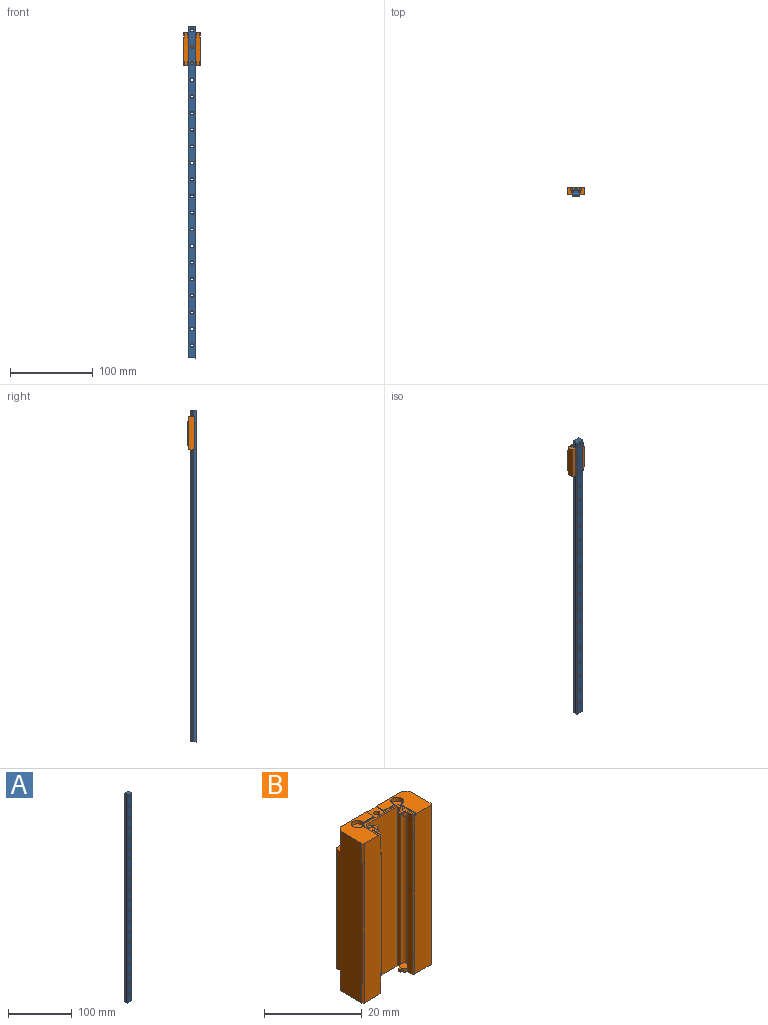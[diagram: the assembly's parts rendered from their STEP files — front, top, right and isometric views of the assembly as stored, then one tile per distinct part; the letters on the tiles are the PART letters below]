
ASSEMBLY  parts=2 mates=1
PART A: 122 faces, bbox 9x6.5x400 mm
  f0: cylinder r=1.75mm len=3.5mm, axis (0,1,0), area 30.8mm2, adj f45,f58
  f1: cylinder r=1.75mm len=3.5mm, axis (0,1,0), area 30.8mm2, adj f43,f56
  f2: cylinder r=1.75mm len=3.5mm, axis (0,1,0), area 30.8mm2, adj f41,f54
  f3: cylinder r=1.75mm len=3.5mm, axis (0,1,0), area 30.8mm2, adj f39,f52
  f4: cylinder r=1.75mm len=3.5mm, axis (0,1,0), area 30.8mm2, adj f37,f50
  f5: cylinder r=1.75mm len=3.5mm, axis (0,1,0), area 30.8mm2, adj f35,f48
  f6: cylinder r=1.75mm len=3.5mm, axis (0,1,0), area 30.8mm2, adj f33,f46
  f7: cylinder r=1.75mm len=3.5mm, axis (0,1,0), area 30.8mm2, adj f29,f30
  f8: cylinder r=1mm len=400mm, axis (0,0,-1), area 461.1mm2, adj f9,f27,f72,f121
  f9: plane 400x0.5mm, normal (0,-1,0), area 200mm2, adj f8,f10,f72,f121
  f10: plane 400x0.5mm, normal (-1,0,0), area 200mm2, adj f9,f11,f72,f121
  f11: plane 400x0.47mm, normal (0,1,0), area 187.1mm2, adj f10,f12,f72,f121
  f12: cylinder r=1mm len=400mm, axis (0,0,-1), area 512.8mm2, adj f11,f13,f72,f121
  f13: plane 400x3.51mm, normal (-1,0,0), area 1402mm2, adj f12,f14,f72,f121
  f14: plane 400x0.2mm, normal (-0.71,-0.71,0), area 113.1mm2, adj f13,f15,f72,f121
  f15: plane 400x8.6mm, normal (0,-1,0), area 3201.1mm2, adj f14,f16,f30,f46,f48,f50,f52,f54
  f16: plane 400x0.2mm, normal (0.71,-0.71,0), area 113.1mm2, adj f15,f17,f72,f121
  f17: plane 400x3.51mm, normal (1,0,0), area 1402mm2, adj f16,f18,f72,f121
  f18: cylinder r=1mm len=400mm, axis (0,0,-1), area 512.8mm2, adj f17,f19,f72,f121
  f19: plane 400x0.47mm, normal (0,1,0), area 187.1mm2, adj f18,f20,f72,f121
  f20: plane 400x0.5mm, normal (1,0,0), area 200mm2, adj f19,f21,f72,f121
  f21: plane 400x0.5mm, normal (0,-1,0), area 200mm2, adj f20,f22,f72,f121
  f22: cylinder r=1mm len=400mm, axis (0,0,-1), area 461.1mm2, adj f21,f23,f72,f121
  f23: plane 400x0.61mm, normal (1,0,0), area 242mm2, adj f22,f24,f72,f121
  f24: plane 400x0.2mm, normal (0.71,0.71,0), area 113.1mm2, adj f23,f25,f72,f121
  f25: plane 400x8.6mm, normal (0,1,0), area 2796.6mm2, adj f24,f26,f31,f47,f49,f51,f53,f55
  f26: plane 400x0.2mm, normal (-0.71,0.71,0), area 113.1mm2, adj f25,f27,f72,f121
  f27: plane 400x0.61mm, normal (-1,0,0), area 242mm2, adj f8,f26,f72,f121
  f28: cylinder r=3mm len=6mm, axis (0,1,0), area 62.2mm2, adj f29,f31
  f29: plane 6x6mm, normal (0,1,0), area 18.7mm2, adj f7,f28
  f30: cone r=1.75mm half-angle=45deg, axis (0,-1,0), area 3.3mm2, adj f7,f15
  f31: cone r=3mm half-angle=45deg, axis (0,1,0), area 5.5mm2, adj f25,f28
  f32: cylinder r=3mm len=6mm, axis (0,1,0), area 62.2mm2, adj f33,f47
  f33: plane 6x6mm, normal (0,1,0), area 18.7mm2, adj f6,f32
  f34: cylinder r=3mm len=6mm, axis (0,1,0), area 62.2mm2, adj f35,f49
  f35: plane 6x6mm, normal (0,1,0), area 18.7mm2, adj f5,f34
  f36: cylinder r=3mm len=6mm, axis (0,1,0), area 62.2mm2, adj f37,f51
  f37: plane 6x6mm, normal (0,1,0), area 18.7mm2, adj f4,f36
  f38: cylinder r=3mm len=6mm, axis (0,1,0), area 62.2mm2, adj f39,f53
  f39: plane 6x6mm, normal (0,1,0), area 18.7mm2, adj f3,f38
  f40: cylinder r=3mm len=6mm, axis (0,1,0), area 62.2mm2, adj f41,f55
  f41: plane 6x6mm, normal (0,1,0), area 18.7mm2, adj f2,f40
  f42: cylinder r=3mm len=6mm, axis (0,1,0), area 62.2mm2, adj f43,f57
  f43: plane 6x6mm, normal (0,1,0), area 18.7mm2, adj f1,f42
  f44: cylinder r=3mm len=6mm, axis (0,1,0), area 62.2mm2, adj f45,f59
  f45: plane 6x6mm, normal (0,1,0), area 18.7mm2, adj f0,f44
  f46: cone r=1.75mm half-angle=45deg, axis (0,-1,0), area 3.3mm2, adj f6,f15
  f47: cone r=3mm half-angle=45deg, axis (0,1,0), area 5.5mm2, adj f25,f32
  f48: cone r=1.75mm half-angle=45deg, axis (0,-1,0), area 3.3mm2, adj f5,f15
  f49: cone r=3mm half-angle=45deg, axis (0,1,0), area 5.5mm2, adj f25,f34
  f50: cone r=1.75mm half-angle=45deg, axis (0,-1,0), area 3.3mm2, adj f4,f15
  f51: cone r=3mm half-angle=45deg, axis (0,1,0), area 5.5mm2, adj f25,f36
  f52: cone r=1.75mm half-angle=45deg, axis (0,-1,0), area 3.3mm2, adj f3,f15
  f53: cone r=3mm half-angle=45deg, axis (0,1,0), area 5.5mm2, adj f25,f38
  f54: cone r=1.75mm half-angle=45deg, axis (0,-1,0), area 3.3mm2, adj f2,f15
  f55: cone r=3mm half-angle=45deg, axis (0,1,0), area 5.5mm2, adj f25,f40
  f56: cone r=1.75mm half-angle=45deg, axis (0,-1,0), area 3.3mm2, adj f1,f15
  f57: cone r=3mm half-angle=45deg, axis (0,1,0), area 5.5mm2, adj f25,f42
  f58: cone r=1.75mm half-angle=45deg, axis (0,-1,0), area 3.3mm2, adj f0,f15
  f59: cone r=3mm half-angle=45deg, axis (0,1,0), area 5.5mm2, adj f25,f44
  f60: cylinder r=1.75mm len=3.5mm, axis (0,1,0), area 30.8mm2, adj f98,f119
  f61: cylinder r=1.75mm len=3.5mm, axis (0,1,0), area 30.8mm2, adj f96,f117
  f62: cylinder r=1.75mm len=3.5mm, axis (0,1,0), area 30.8mm2, adj f94,f115
  f63: cylinder r=1.75mm len=3.5mm, axis (0,1,0), area 30.8mm2, adj f92,f113
  f64: cylinder r=1.75mm len=3.5mm, axis (0,1,0), area 30.8mm2, adj f90,f111
  f65: cylinder r=1.75mm len=3.5mm, axis (0,1,0), area 30.8mm2, adj f88,f109
  f66: cylinder r=1.75mm len=3.5mm, axis (0,1,0), area 30.8mm2, adj f86,f107
  f67: cylinder r=1.75mm len=3.5mm, axis (0,1,0), area 30.8mm2, adj f84,f105
  f68: cylinder r=1.75mm len=3.5mm, axis (0,1,0), area 30.8mm2, adj f82,f103
  f69: cylinder r=1.75mm len=3.5mm, axis (0,1,0), area 30.8mm2, adj f80,f101
  f70: cylinder r=1.75mm len=3.5mm, axis (0,1,0), area 30.8mm2, adj f78,f99
  f71: cylinder r=1.75mm len=3.5mm, axis (0,1,0), area 30.8mm2, adj f74,f75
  f72: plane 9x6.5mm, normal (0,0,-1), area 55.2mm2, adj f8,f9,f10,f11,f12,f13,f14,f15
  f73: cylinder r=3mm len=6mm, axis (0,1,0), area 62.2mm2, adj f74,f76
  f74: plane 6x6mm, normal (0,1,0), area 18.7mm2, adj f71,f73
  f75: cone r=1.75mm half-angle=45deg, axis (0,-1,0), area 3.3mm2, adj f15,f71
  f76: cone r=3mm half-angle=45deg, axis (0,1,0), area 5.5mm2, adj f25,f73
  f77: cylinder r=3mm len=6mm, axis (0,1,0), area 62.2mm2, adj f78,f100
  f78: plane 6x6mm, normal (0,1,0), area 18.7mm2, adj f70,f77
  f79: cylinder r=3mm len=6mm, axis (0,1,0), area 62.2mm2, adj f80,f102
  f80: plane 6x6mm, normal (0,1,0), area 18.7mm2, adj f69,f79
  f81: cylinder r=3mm len=6mm, axis (0,1,0), area 62.2mm2, adj f82,f104
  f82: plane 6x6mm, normal (0,1,0), area 18.7mm2, adj f68,f81
  f83: cylinder r=3mm len=6mm, axis (0,1,0), area 62.2mm2, adj f84,f106
  f84: plane 6x6mm, normal (0,1,0), area 18.7mm2, adj f67,f83
  f85: cylinder r=3mm len=6mm, axis (0,1,0), area 62.2mm2, adj f86,f108
  f86: plane 6x6mm, normal (0,1,0), area 18.7mm2, adj f66,f85
  f87: cylinder r=3mm len=6mm, axis (0,1,0), area 62.2mm2, adj f88,f110
  f88: plane 6x6mm, normal (0,1,0), area 18.7mm2, adj f65,f87
  f89: cylinder r=3mm len=6mm, axis (0,1,0), area 62.2mm2, adj f90,f112
  f90: plane 6x6mm, normal (0,1,0), area 18.7mm2, adj f64,f89
  f91: cylinder r=3mm len=6mm, axis (0,1,0), area 62.2mm2, adj f92,f114
  f92: plane 6x6mm, normal (0,1,0), area 18.7mm2, adj f63,f91
  f93: cylinder r=3mm len=6mm, axis (0,1,0), area 62.2mm2, adj f94,f116
  f94: plane 6x6mm, normal (0,1,0), area 18.7mm2, adj f62,f93
  f95: cylinder r=3mm len=6mm, axis (0,1,0), area 62.2mm2, adj f96,f118
  f96: plane 6x6mm, normal (0,1,0), area 18.7mm2, adj f61,f95
  f97: cylinder r=3mm len=6mm, axis (0,1,0), area 62.2mm2, adj f98,f120
  f98: plane 6x6mm, normal (0,1,0), area 18.7mm2, adj f60,f97
  f99: cone r=1.75mm half-angle=45deg, axis (0,-1,0), area 3.3mm2, adj f15,f70
  f100: cone r=3mm half-angle=45deg, axis (0,1,0), area 5.5mm2, adj f25,f77
  f101: cone r=1.75mm half-angle=45deg, axis (0,-1,0), area 3.3mm2, adj f15,f69
  f102: cone r=3mm half-angle=45deg, axis (0,1,0), area 5.5mm2, adj f25,f79
  f103: cone r=1.75mm half-angle=45deg, axis (0,-1,0), area 3.3mm2, adj f15,f68
  f104: cone r=3mm half-angle=45deg, axis (0,1,0), area 5.5mm2, adj f25,f81
  f105: cone r=1.75mm half-angle=45deg, axis (0,-1,0), area 3.3mm2, adj f15,f67
  f106: cone r=3mm half-angle=45deg, axis (0,1,0), area 5.5mm2, adj f25,f83
  f107: cone r=1.75mm half-angle=45deg, axis (0,-1,0), area 3.3mm2, adj f15,f66
  f108: cone r=3mm half-angle=45deg, axis (0,1,0), area 5.5mm2, adj f25,f85
  f109: cone r=1.75mm half-angle=45deg, axis (0,-1,0), area 3.3mm2, adj f15,f65
  f110: cone r=3mm half-angle=45deg, axis (0,1,0), area 5.5mm2, adj f25,f87
  f111: cone r=1.75mm half-angle=45deg, axis (0,-1,0), area 3.3mm2, adj f15,f64
  f112: cone r=3mm half-angle=45deg, axis (0,1,0), area 5.5mm2, adj f25,f89
  f113: cone r=1.75mm half-angle=45deg, axis (0,-1,0), area 3.3mm2, adj f15,f63
  f114: cone r=3mm half-angle=45deg, axis (0,1,0), area 5.5mm2, adj f25,f91
  f115: cone r=1.75mm half-angle=45deg, axis (0,-1,0), area 3.3mm2, adj f15,f62
  f116: cone r=3mm half-angle=45deg, axis (0,1,0), area 5.5mm2, adj f25,f93
  f117: cone r=1.75mm half-angle=45deg, axis (0,-1,0), area 3.3mm2, adj f15,f61
  f118: cone r=3mm half-angle=45deg, axis (0,1,0), area 5.5mm2, adj f25,f95
  f119: cone r=1.75mm half-angle=45deg, axis (0,-1,0), area 3.3mm2, adj f15,f60
  f120: cone r=3mm half-angle=45deg, axis (0,1,0), area 5.5mm2, adj f25,f97
  f121: plane 9x6.5mm, normal (0,0,1), area 55.2mm2, adj f8,f9,f10,f11,f12,f13,f14,f15
PART B: 137 faces, bbox 20x8x39.9 mm
  f0: plane 0.4x0.4mm, normal (0,0,1), area 0mm2, adj f17,f18,f36,f114
  f1: plane 5.5x1.3mm, normal (0,0,1), area 2.1mm2, adj f18,f24,f25,f26,f37,f110
  f2: plane 5.5x1.3mm, normal (0,0,1), area 2.1mm2, adj f20,f23,f25,f27,f34,f109
  f3: plane 0.4x0.4mm, normal (0,0,1), area 0mm2, adj f19,f20,f35,f112
  f4: plane 0.4x0.4mm, normal (0,0,1), area 0mm2, adj f19,f28,f39,f111
  f5: plane 0.4x0.4mm, normal (0,0,1), area 0mm2, adj f17,f21,f38,f113
  f6: plane 0.4x0.4mm, normal (0,0,-1), area 0mm2, adj f17,f21,f38,f50
  f7: plane 0.4x0.4mm, normal (0,0,-1), area 0mm2, adj f19,f28,f39,f51
  f8: plane 0.4x0.4mm, normal (0,0,-1), area 0mm2, adj f19,f20,f35,f52
  f9: plane 5.5x1.3mm, normal (0,0,-1), area 2.1mm2, adj f20,f23,f25,f27,f34,f48
  f10: plane 5.5x1.3mm, normal (0,0,-1), area 2.1mm2, adj f18,f24,f25,f26,f37,f47
  f11: plane 3x3mm, normal (0,1,0), area 7.1mm2, adj f13
  f12: plane 3x3mm, normal (0,1,0), area 7.1mm2, adj f14
  f13: cylinder r=1.5mm len=3mm, axis (0,1,0), area 25.4mm2, adj f11,f15
  f14: cylinder r=1.5mm len=3mm, axis (0,1,0), area 25.4mm2, adj f12,f16
  f15: cone r=1.5mm half-angle=45deg, axis (0,1,0), area 4.4mm2, adj f13,f23
  f16: cone r=1.5mm half-angle=45deg, axis (0,1,0), area 4.4mm2, adj f14,f24
  f17: plane 39.9x4.9mm, normal (0,-1,0), area 193.3mm2, adj f0,f5,f6,f36,f38,f46,f49,f50
  f18: plane 39.9x7.4mm, normal (-1,0,0), area 284.3mm2, adj f0,f1,f10,f36,f37,f46,f47,f49
  f19: plane 39.9x4.9mm, normal (0,-1,0), area 193.3mm2, adj f3,f4,f7,f8,f35,f39,f51,f52
  f20: plane 39.9x7.4mm, normal (1,0,0), area 284.3mm2, adj f2,f3,f8,f9,f34,f35,f48,f52
  f21: plane 39.9x1.41mm, normal (1,0,0), area 55.1mm2, adj f5,f6,f31,f38,f50,f56,f64,f95
  f22: plane 39.9x0.81mm, normal (-1,0,0), area 32.1mm2, adj f29,f33,f56,f59,f95,f98
  f23: plane 29.9x4.9mm, normal (0,1,0), area 126.2mm2, adj f2,f9,f15,f27,f34,f44
  f24: plane 29.9x4.9mm, normal (0,1,0), area 126.2mm2, adj f1,f10,f16,f26,f37,f45
  f25: plane 39.9x18mm, normal (0,1,0), area 448mm2, adj f1,f2,f9,f10,f26,f27,f47,f48
  f26: plane 29.9x0.3mm, normal (0.71,0.71,0), area 12.7mm2, adj f1,f10,f24,f25
  f27: plane 29.9x0.3mm, normal (-0.71,0.71,0), area 12.7mm2, adj f2,f9,f23,f25
  f28: plane 39.9x1.41mm, normal (-1,0,0), area 55.1mm2, adj f4,f7,f29,f39,f51,f56,f63,f95
  f29: cylinder r=1mm len=38.1mm, axis (0,0,-1), area 127.3mm2, adj f22,f28,f53,f93
  f30: plane 39.9x0.81mm, normal (1,0,0), area 32.1mm2, adj f31,f33,f56,f68,f95,f107
  f31: cylinder r=1mm len=38.1mm, axis (0,0,-1), area 127.3mm2, adj f21,f30,f54,f92
  f32: cylinder r=0.64mm len=39.5mm, axis (0,0,-1), area 159.8mm2, adj f75,f120
  f33: plane 39.9x9mm, normal (0,-1,0), area 359.1mm2, adj f22,f30,f56,f95
  f34: plane 29.9x0.3mm, normal (0.71,0.71,0), area 12.7mm2, adj f2,f9,f20,f23
  f35: plane 29.9x0.3mm, normal (0.71,-0.71,0), area 12.7mm2, adj f3,f8,f19,f20
  f36: plane 29.9x0.3mm, normal (-0.71,-0.71,0), area 12.7mm2, adj f0,f17,f18,f46
  f37: plane 29.9x0.3mm, normal (-0.71,0.71,0), area 12.7mm2, adj f1,f10,f18,f24
  f38: plane 29.9x0.3mm, normal (0.71,-0.71,0), area 12.7mm2, adj f5,f6,f17,f21
  f39: plane 29.9x0.3mm, normal (-0.71,-0.71,0), area 12.7mm2, adj f4,f7,f19,f28
  f40: plane 3x3mm, normal (0,1,0), area 7.1mm2, adj f42
  f41: plane 3x3mm, normal (0,1,0), area 7.1mm2, adj f43
  f42: cylinder r=1.5mm len=3mm, axis (0,1,0), area 25.4mm2, adj f40,f44
  f43: cylinder r=1.5mm len=3mm, axis (0,1,0), area 25.4mm2, adj f41,f45
  f44: cone r=1.5mm half-angle=45deg, axis (0,1,0), area 4.4mm2, adj f23,f42
  f45: cone r=1.5mm half-angle=45deg, axis (0,1,0), area 4.4mm2, adj f24,f43
  f46: plane 0.4x0.4mm, normal (0,0,-1), area 0mm2, adj f17,f18,f36,f49
  f47: plane 5x1mm, normal (-0.71,0.71,0), area 7.1mm2, adj f10,f18,f25,f58
  f48: plane 5x1mm, normal (0.71,0.71,0), area 7.1mm2, adj f9,f20,f25,f55
  f49: plane 5x0.4mm, normal (-0.71,-0.71,0), area 2.8mm2, adj f17,f18,f46,f58
  f50: plane 5x0.4mm, normal (0.71,-0.71,0), area 2.8mm2, adj f6,f17,f21,f56
  f51: plane 5x0.4mm, normal (-0.71,-0.71,0), area 2.8mm2, adj f7,f19,f28,f56
  f52: plane 5x0.4mm, normal (0.71,-0.71,0), area 2.8mm2, adj f8,f19,f20,f55
  f53: plane 2.47x2mm, normal (0,0,1), area 3.4mm2, adj f29,f59,f60,f61,f62,f63
  f54: plane 2.47x2mm, normal (0,0,1), area 3.4mm2, adj f31,f64,f65,f66,f67,f68
  f55: plane 8.58x7.7mm, normal (0,0,-1), area 38.3mm2, adj f19,f20,f25,f48,f52,f69,f71,f72
  f56: plane 10x5mm, normal (0,0,-1), area 10.9mm2, adj f17,f19,f21,f22,f28,f30,f33,f50
  f57: cylinder r=1.3mm len=2.6mm, axis (0,0,1), area 7.1mm2, adj f56,f58,f73,f74,f75,f78,f79,f82
  f58: plane 8.58x7.7mm, normal (0,0,-1), area 38.3mm2, adj f17,f18,f25,f47,f49,f57,f70,f74
  f59: cylinder r=1mm len=0.9mm, axis (0,0,1), area 1.1mm2, adj f22,f53,f56,f60
  f60: plane 0.9x0.5mm, normal (0,1,0), area 0.4mm2, adj f53,f56,f59,f61
  f61: plane 0.9x0.5mm, normal (-1,0,0), area 0.4mm2, adj f53,f56,f60,f62
  f62: plane 0.9x0.5mm, normal (0,-1,0), area 0.4mm2, adj f53,f56,f61,f63
  f63: cylinder r=1mm len=0.9mm, axis (0,0,1), area 1.1mm2, adj f28,f53,f56,f62
  f64: cylinder r=1mm len=0.9mm, axis (0,0,1), area 1.1mm2, adj f21,f54,f56,f65
  f65: plane 0.9x0.5mm, normal (0,-1,0), area 0.4mm2, adj f54,f56,f64,f66
  f66: plane 0.9x0.5mm, normal (1,0,0), area 0.4mm2, adj f54,f56,f65,f67
  f67: plane 0.9x0.5mm, normal (0,1,0), area 0.4mm2, adj f54,f56,f66,f68
  f68: cylinder r=1mm len=0.9mm, axis (0,0,1), area 1.1mm2, adj f30,f54,f56,f67
  f69: cylinder r=1.3mm len=2.6mm, axis (0,0,1), area 7.1mm2, adj f55,f56,f72,f73,f75,f85,f86,f89
  f70: plane 2.2x0.2mm, normal (1,0,0), area 0.4mm2, adj f25,f58,f74,f75
  f71: plane 2.2x0.2mm, normal (-1,0,0), area 0.4mm2, adj f25,f55,f72,f75
  f72: plane 3.09x0.2mm, normal (0,-1,0), area 0.6mm2, adj f55,f69,f71,f75
  f73: plane 9.63x0.2mm, normal (0,1,0), area 1.9mm2, adj f56,f57,f69,f75
  f74: plane 3.09x0.2mm, normal (0,-1,0), area 0.6mm2, adj f57,f58,f70,f75
  f75: plane 9.63x2.7mm, normal (0,0,-1), area 9.6mm2, adj f25,f32,f57,f69,f70,f71,f72,f73
  f76: plane 0.45x0.2mm, normal (0,1,0), area 0.1mm2, adj f56,f77,f81,f82
  f77: plane 2.2x0.2mm, normal (-1,0,0), area 0.4mm2, adj f17,f56,f76,f82
  f78: plane 4.64x0.2mm, normal (1,0,0), area 0.9mm2, adj f17,f57,f58,f82
  f79: plane 1.65x0.2mm, normal (-1,0,0), area 0.3mm2, adj f56,f57,f80,f82
  f80: plane 0.4x0.2mm, normal (0,-1,0), area 0.1mm2, adj f56,f79,f81,f82
  f81: cylinder r=0.5mm len=1mm, axis (0,0,-1), area 0.3mm2, adj f56,f76,f80,f82
  f82: plane 4.85x1.4mm, normal (0,0,-1), area 3.2mm2, adj f17,f57,f76,f77,f78,f79,f80,f81
  f83: cylinder r=0.5mm len=1mm, axis (0,0,-1), area 0.3mm2, adj f56,f84,f88,f89
  f84: plane 0.4x0.2mm, normal (0,-1,0), area 0.1mm2, adj f56,f83,f85,f89
  f85: plane 1.65x0.2mm, normal (1,0,0), area 0.3mm2, adj f56,f69,f84,f89
  f86: plane 4.64x0.2mm, normal (-1,0,0), area 0.9mm2, adj f19,f55,f69,f89
  f87: plane 2.2x0.2mm, normal (1,0,0), area 0.4mm2, adj f19,f56,f88,f89
  f88: plane 0.45x0.2mm, normal (0,1,0), area 0.1mm2, adj f56,f83,f87,f89
  f89: plane 4.85x1.4mm, normal (0,0,-1), area 3.2mm2, adj f19,f69,f83,f84,f85,f86,f87,f88
  f90: plane 2.6x2.6mm, normal (0,0,-1), area 5.3mm2, adj f57
  f91: plane 2.6x2.6mm, normal (0,0,-1), area 5.3mm2, adj f69
  f92: plane 2.47x2mm, normal (0,0,-1), area 3.4mm2, adj f31,f103,f104,f105,f106,f107
  f93: plane 2.47x2mm, normal (0,0,-1), area 3.4mm2, adj f29,f98,f99,f100,f101,f102
  f94: plane 8.58x7.7mm, normal (0,0,1), area 38.3mm2, adj f19,f20,f25,f108,f109,f112,f116,f117
  f95: plane 10x5mm, normal (0,0,1), area 10.9mm2, adj f17,f19,f21,f22,f28,f30,f33,f96
  f96: cylinder r=1.3mm len=2.6mm, axis (0,0,-1), area 7.1mm2, adj f95,f97,f118,f119,f120,f123,f124,f127
  f97: plane 8.58x7.7mm, normal (0,0,1), area 38.3mm2, adj f17,f18,f25,f96,f110,f114,f115,f119
  f98: cylinder r=1mm len=0.9mm, axis (0,0,-1), area 1.1mm2, adj f22,f93,f95,f99
  f99: plane 0.9x0.5mm, normal (0,1,0), area 0.4mm2, adj f93,f95,f98,f100
  f100: plane 0.9x0.5mm, normal (-1,0,0), area 0.4mm2, adj f93,f95,f99,f101
  f101: plane 0.9x0.5mm, normal (0,-1,0), area 0.4mm2, adj f93,f95,f100,f102
  f102: cylinder r=1mm len=0.9mm, axis (0,0,-1), area 1.1mm2, adj f28,f93,f95,f101
  f103: cylinder r=1mm len=0.9mm, axis (0,0,-1), area 1.1mm2, adj f21,f92,f95,f104
  f104: plane 0.9x0.5mm, normal (0,-1,0), area 0.4mm2, adj f92,f95,f103,f105
  f105: plane 0.9x0.5mm, normal (1,0,0), area 0.4mm2, adj f92,f95,f104,f106
  f106: plane 0.9x0.5mm, normal (0,1,0), area 0.4mm2, adj f92,f95,f105,f107
  f107: cylinder r=1mm len=0.9mm, axis (0,0,-1), area 1.1mm2, adj f30,f92,f95,f106
  f108: cylinder r=1.3mm len=2.6mm, axis (0,0,-1), area 7.1mm2, adj f94,f95,f117,f118,f120,f130,f131,f134
  f109: plane 5x1mm, normal (0.71,0.71,0), area 7.1mm2, adj f2,f20,f25,f94
  f110: plane 5x1mm, normal (-0.71,0.71,0), area 7.1mm2, adj f1,f18,f25,f97
  f111: plane 5x0.4mm, normal (-0.71,-0.71,0), area 2.8mm2, adj f4,f19,f28,f95
  f112: plane 5x0.4mm, normal (0.71,-0.71,0), area 2.8mm2, adj f3,f19,f20,f94
  f113: plane 5x0.4mm, normal (0.71,-0.71,0), area 2.8mm2, adj f5,f17,f21,f95
  f114: plane 5x0.4mm, normal (-0.71,-0.71,0), area 2.8mm2, adj f0,f17,f18,f97
  f115: plane 2.2x0.2mm, normal (1,0,0), area 0.4mm2, adj f25,f97,f119,f120
  f116: plane 2.2x0.2mm, normal (-1,0,0), area 0.4mm2, adj f25,f94,f117,f120
  f117: plane 3.09x0.2mm, normal (0,-1,0), area 0.6mm2, adj f94,f108,f116,f120
  f118: plane 9.63x0.2mm, normal (0,1,0), area 1.9mm2, adj f95,f96,f108,f120
  f119: plane 3.09x0.2mm, normal (0,-1,0), area 0.6mm2, adj f96,f97,f115,f120
  f120: plane 9.63x2.7mm, normal (0,0,1), area 9.6mm2, adj f25,f32,f96,f108,f115,f116,f117,f118
  f121: plane 0.45x0.2mm, normal (0,1,0), area 0.1mm2, adj f95,f122,f126,f127
  f122: plane 2.2x0.2mm, normal (-1,0,0), area 0.4mm2, adj f17,f95,f121,f127
  f123: plane 4.64x0.2mm, normal (1,0,0), area 0.9mm2, adj f17,f96,f97,f127
  f124: plane 1.65x0.2mm, normal (-1,0,0), area 0.3mm2, adj f95,f96,f125,f127
  f125: plane 0.4x0.2mm, normal (0,-1,0), area 0.1mm2, adj f95,f124,f126,f127
  f126: cylinder r=0.5mm len=1mm, axis (0,0,1), area 0.3mm2, adj f95,f121,f125,f127
  f127: plane 4.85x1.4mm, normal (0,0,1), area 3.2mm2, adj f17,f96,f121,f122,f123,f124,f125,f126
  f128: cylinder r=0.5mm len=1mm, axis (0,0,1), area 0.3mm2, adj f95,f129,f133,f134
  f129: plane 0.4x0.2mm, normal (0,-1,0), area 0.1mm2, adj f95,f128,f130,f134
  f130: plane 1.65x0.2mm, normal (1,0,0), area 0.3mm2, adj f95,f108,f129,f134
  f131: plane 4.64x0.2mm, normal (-1,0,0), area 0.9mm2, adj f19,f94,f108,f134
  f132: plane 2.2x0.2mm, normal (1,0,0), area 0.4mm2, adj f19,f95,f133,f134
  f133: plane 0.45x0.2mm, normal (0,1,0), area 0.1mm2, adj f95,f128,f132,f134
  f134: plane 4.85x1.4mm, normal (0,0,1), area 3.2mm2, adj f19,f108,f128,f129,f130,f131,f132,f133
  f135: plane 2.6x2.6mm, normal (0,0,1), area 5.3mm2, adj f108
  f136: plane 2.6x2.6mm, normal (0,0,1), area 5.3mm2, adj f96
PLACE A t=(-27.37,-0.93,9.7)mm
PLACE B t=(-27.39,1.88,381.46)mm
MATE slider B.f56 <-> A.f72  axis (0,0,1) through (-30.52,0.33,361.51)mm
